# Revit family: 2069376 Sylvania Lighting Fixture PIXER RECESSED 600X600 HO 4P 4000K9 DALI EM
name_source: partatom
category: Lighting Fixtures
revit_build: Autodesk Revit 2016 (Build: 20150220_1215(x64)
units: mm (PartAtom-declared; Revit-internal decimal feet)

## family parameters
Cut with Voids When Loaded = No
Host = Face
Light Source = No
OmniClass Number = 23.80.70.00
OmniClass Title = Lighting
Part Type = Normal
Room Calculation Point = No
Round Connector Dimension = Use Diameter
Shared = No

## types (2) — shared parameters
Assembly Code = D5020200
AssetType = Fixed
ClassificationName = Uniclass2015
ClassificationValue = EF_70_80
Default Elevation = 1219 mm
Description = PIXER RECESSED 600X600 HO 4P 4000K9 DALI EM is a high performance low glare office luminaire with individually adjustable light pods to enhance arhitectural design. Diffuser is made of optical grade polycarbonate with an optical film for high efficacy and excellent glare control. Suitable for offices where aesthetics is important. Ceiling recessed 600x600mm, White colour - RAL9010. DALI dimmable, 4000K Neutral White LED, CRI>90, chromaticity tolerance of 3-step MacAdam ellipse. Lumen package of 4150 lm, total power consumtion 39W, efficacy 106lm/W. Lumen maintenance of L90B10 at 61,000 hours. UGR<19. IK02, IP20. Electrical protection: Class II. 3hr maintained emergency lighting. Glow wire test 650°C.
DimmingControlOptions = Dimmable
DocumentationLiterature = http://www.sylvania-lighting.com
ElectricShockClassification = Class II
IfcExportAs = IfcLightFixtureType
IfcExportType = IfcLightFixtureType
ImpactProtectionIndex = IK02
IngressProtection = IP20
InputNominalFrequency = 50/60 Hz
InputVoltage = 220-240V~
Keynote = 16500
Lamp = LED
LampColourRenderingIndex = 90
LampColourTemperature = 4000 K
LampMacAdamStep = 3
LampsType = LED
Length_SYL = 595 mm  [stored 1.9521 ft]
LightOutputRatio = 100
Manufacturer = Feilo Sylvania
ManufacturerName = Feilo Sylvania
Material = powder coated steel housing, polycarbonate diffuser
Material_1_SYL = PC/ABS Plastic
Model = PIXER RECESSED 600X600 HO 4P 4000K9 DALI EM
ModelNumber = 2069376
ModelReference = PIXER RECESSED 600X600 HO 4P 4000K9 DALI EM
Name = PIXER RECESSED 600X600 HO 4P 4000K9 DALI EM
NominalDepth = 595 mm  [stored 1.9521 ft]
NominalHeight = 75 mm
NominalLength = 595 mm  [stored 1.9521 ft]
PodXInstance_SYL = 2
PowerConsumption = 39 W
PowerFactor = 0.94
RadiusBody_SYL = 5 mm  [stored 0.0164042 ft]
Type Image = <None>
TypeName = PIXER RECESSED 600X600 HO 4P 4000K9 DALI EM
URL = http://www.sylvania-lighting.com
Voltage = 230 V
Weight = 6.2 kg
Width_SYL = 595 mm  [stored 1.9521 ft]
Xdistance_SYL = 149 mm
Xinstance_SYL = 4
Ydistance_SYL = 149 mm
Yinstance_SYL = 4
zero-valued in all types: Cost

## per-type parameters (varying)
| type | Apparent Load | LampNominalLuminous | LuminousEfficacy | TypePod_SYL |
| 2069376 PIXER R 600 HO 4P 4K9 DALI EM | 39 VA | 4152 lm | 106 lm/W | Pixer Pod Square : 2069376 PIXER R 600 HO 4P 4K9 DALI EM |
| 2069376 PIXER R 600 HO 4P 4K9 DALI EM Emergency mode | 3 VA | 80.1 lm | 28.61 lm/W | Pixer Pod Square : 2069376 PIXER R 600 HO 4P 4K9 DALI EM Emergency mode |

note: [stored X ft] marks values corroborated as IEEE doubles in the binary element streams (Revit-internal decimal feet)

## geometry (parser evidence)
native form markers: Sweep x3
no freeform markers — native parametric forms only
